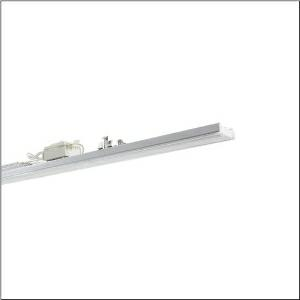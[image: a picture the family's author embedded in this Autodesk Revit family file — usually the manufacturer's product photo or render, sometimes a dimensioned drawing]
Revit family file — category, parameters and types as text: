
# Revit family: licross_11_recessed_mo_51te11dn4axg
name_source: partatom
category: Lighting Fixtures
units: mm (PartAtom-declared; Revit-internal decimal feet)

## family parameters
Cut with Voids When Loaded = No
Host = Face
Light Source = No
Part Type = Normal
Room Calculation Point = No
Round Connector Dimension = Use Diameter
Shared = No

## types (1)
- --- (1 x LED, 10080 lm, 56.7 W, 4000K)
    Apparent Load = 57 VA
    CIE Flux Codes = 89 96 99 100 100
    Color Rendering = 80
    Color Temperature = 4000K
    Default Elevation = 1800 mm
    Description = Licross 11 Recessed MO, luminaire insert, of sheet steel, galvanised, coil coated, white, length: 1.500mm, width: 66mm, height: 67mm, LED rated luminous flux: 10.080lm, light colour: 840, SDCM (Standard Deviation of Colour Matching)MacAdam ≤ 2 SDCM (initial), control gear: DALI 2, with plug, 5-pole, with phase selection, mains connection: 220..240V, AC, 50/60Hz, rated input power: 57W, internal wiring halogen-free, primary light control with lens, of plastic, primary optical cover: cover, of PMMA, light emission: direct distribution, primary light characteristic: symmetric, protection rating (complete): IP54, insulation class (complete): insulation class I (protective earthing), certification: CE, ENEC, VDE, UKCA, protection symbol: D if used in an environment with non-conductive dust loads with corresponding accessories, impact resistance: IK06, permissible ambient temperature for indoor applications: -25..+35°C, corresponds to IFS (International Featured Standards) requirements for safety and quality in the food industry, reducing of maximum allowable ambient temperature of 5°C with ceiling mounting, LABS conformity tested according to VDMA 24364:2018-05, The light source and the operating device comply with the requirements of the Ecodesign Regulation (EU) 2019/2020 and are replaceable in accordance with this regulation, packaging unit: 1 piece
    Height = 58 mm
    Lamp = 1 x LED
    Lamp Light Flux = 10080 lm
    Lamp Power = 56.7 W
    Lamp count = 1
    Length = 1500 mm
    Luminous efficacy = 178 lm/W
    Manufacturer = Siteco
    ModVariant = No
    Model = 51TE11DN4AXG
    Mounting Place = Ceiling
    Mounting Type = Pendant
    Number of Poles = 1
    OnlyDefault = Yes
    Power Factor = 1
    Product Name = Licross 11 Recessed MO
    Product group = luminaire insert | ceiling pendant
    ProductGroupID = 901
    Protection Class = Protection class I
    Protection Degree = IP 54
    RLX_Detail_Level = 1
    RLX_Emergency_Light_Flux = 0 lm
    RLX_Emergency_Type = 0
    RLX_Emergency_Type_DB = No
    RlxData = <blob elided: 24769 chars, md5=0581d4f2>
    Socket = socket
    Standby Power = 0 W
    System Light Flux = 10080 lm
    System Power = 57 W
    Type Comments = factory setting: luminous flux: 100 % | dim-lin: 254 | 378 mA
    Type Image = l_1296930.jpg
    URL = http://relux.com
    VarID = @adj_100237
    Voltage = 0 V
    Weight = 0.00 kg
    Width = 66 mm

## geometry (parser evidence)
native form markers: Blend x4, Sweep x9
no freeform markers — native parametric forms only
